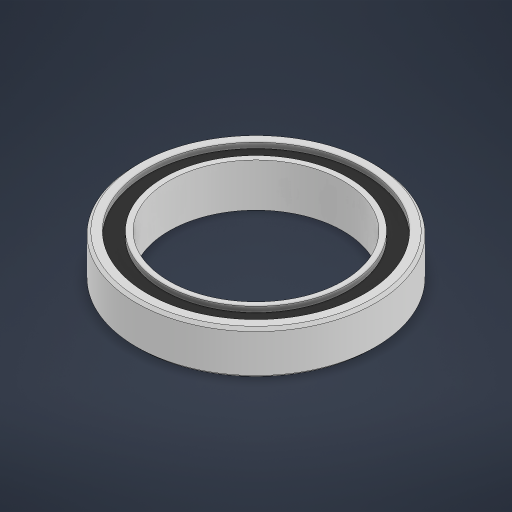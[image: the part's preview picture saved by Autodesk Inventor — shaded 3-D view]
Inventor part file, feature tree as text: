
AUTODESK INVENTOR PART (.ipt)
format: ipt  version: 2024 (Build 280153000, 153)  size: 239,104 bytes
history: native  units: in
note: dims shown in document units (in); Inventor stores cm internally (conversion verified against a paired STEP export)
features: extrude x3, sketch x3, chamfer x1, projected_geometry x1
ambient origin geometry x8: Origin, YZ Plane, XZ Plane, XY Plane, X Axis, Y Axis, Z Axis, Center Point
bodies: Solid1 (feature_tree)
feature tree (8):
  extrude  "Extrusion1"  Depth=0.1575in
  chamfer  "Chamfer1"  Distance=0.1575in
  extrude  "Extrusion2"  Depth=0.0197in
  extrude  "Extrusion3"  Depth=0.0197in TaperAngle=0.0deg
  sketch  "Sketch1"  dims[d0=0.6299in d1=0.8661in d2=0.1575in d3=0.0in]
  sketch  "Sketch2"  dims[d4=0.0098in d5=0.0787in d6=45.0deg d7=0.0197in]
  sketch  "Sketch3"  dims[d8=0.0591in d9=0.0197in d10=0.0in d11=0.0197in d12=0.0in]
  projected_geometry  "Projected Loop1"
